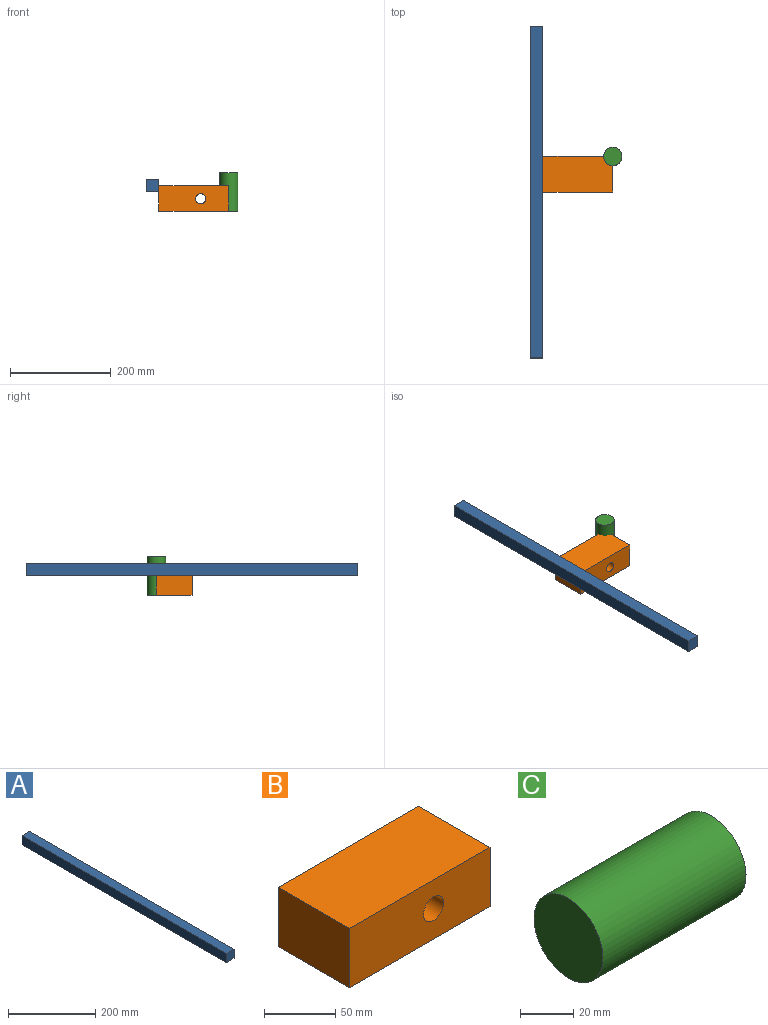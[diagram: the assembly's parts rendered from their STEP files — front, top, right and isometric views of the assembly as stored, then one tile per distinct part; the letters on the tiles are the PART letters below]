
ASSEMBLY  parts=3 mates=2
PART A: 6 faces, bbox 25.4x660.4x25.4 mm
  f0: plane 660.4x25.4mm, normal (0,0,1), area 16774.2mm2, adj f1,f3,f4,f5
  f1: plane 660.4x25.4mm, normal (-1,0,0), area 16774.2mm2, adj f0,f2,f4,f5
  f2: plane 660.4x25.4mm, normal (0,0,-1), area 16774.2mm2, adj f1,f3,f4,f5
  f3: plane 660.4x25.4mm, normal (1,0,0), area 16774.2mm2, adj f0,f2,f4,f5
  f4: plane 25.4x25.4mm, normal (0,-1,0), area 645.2mm2, adj f0,f1,f2,f3
  f5: plane 25.4x25.4mm, normal (0,1,0), area 645.2mm2, adj f0,f1,f2,f3
PART B: 7 faces, bbox 139.1x70.6x50.8 mm
  f0: plane 70.63x50.8mm, normal (-1,0,0), area 3587.8mm2, adj f1,f3,f4,f5
  f1: plane 139.13x50.8mm, normal (0,-1,0), area 6749.8mm2, adj f0,f2,f4,f5,f6
  f2: plane 70.63x50.8mm, normal (1,0,0), area 3587.8mm2, adj f1,f3,f4,f5
  f3: plane 139.13x50.8mm, normal (0,1,0), area 6749.8mm2, adj f0,f2,f4,f5,f6
  f4: plane 139.13x70.63mm, normal (0,0,1), area 9826.1mm2, adj f0,f1,f2,f3
  f5: plane 139.13x70.63mm, normal (0,0,-1), area 9826.1mm2, adj f0,f1,f2,f3
  f6: cylinder r=10.06mm len=70.63mm, axis (0,1,0), area 4463.4mm2, adj f1,f3
PART C: 3 faces, bbox 76.2x36.8x36.8 mm
  f0: cylinder r=18.38mm len=76.2mm, axis (-1,0,0), area 8800.3mm2, adj f1,f2
  f1: plane 36.76x36.76mm, normal (1,0,0), area 1061.4mm2, adj f0
  f2: plane 36.76x36.76mm, normal (-1,0,0), area 1061.4mm2, adj f0
PLACE A rot(axis=(-0.21,0,-0.98),0deg) t=(2.19,398.43,136.09)mm
PLACE B rot(axis=(1,0,0),180deg) t=(27.59,138.85,123.39)mm
PLACE C rot(axis=(0,1,0),90deg) t=(166.72,136.42,148.79)mm
MATE fastened A.f3 <-> B.f0  axis (1,0,0) through (27.59,68.23,123.39)mm
MATE fastened C.f0 <-> B.f4  axis (0,0,-1) through (166.72,138.85,72.59)mm
